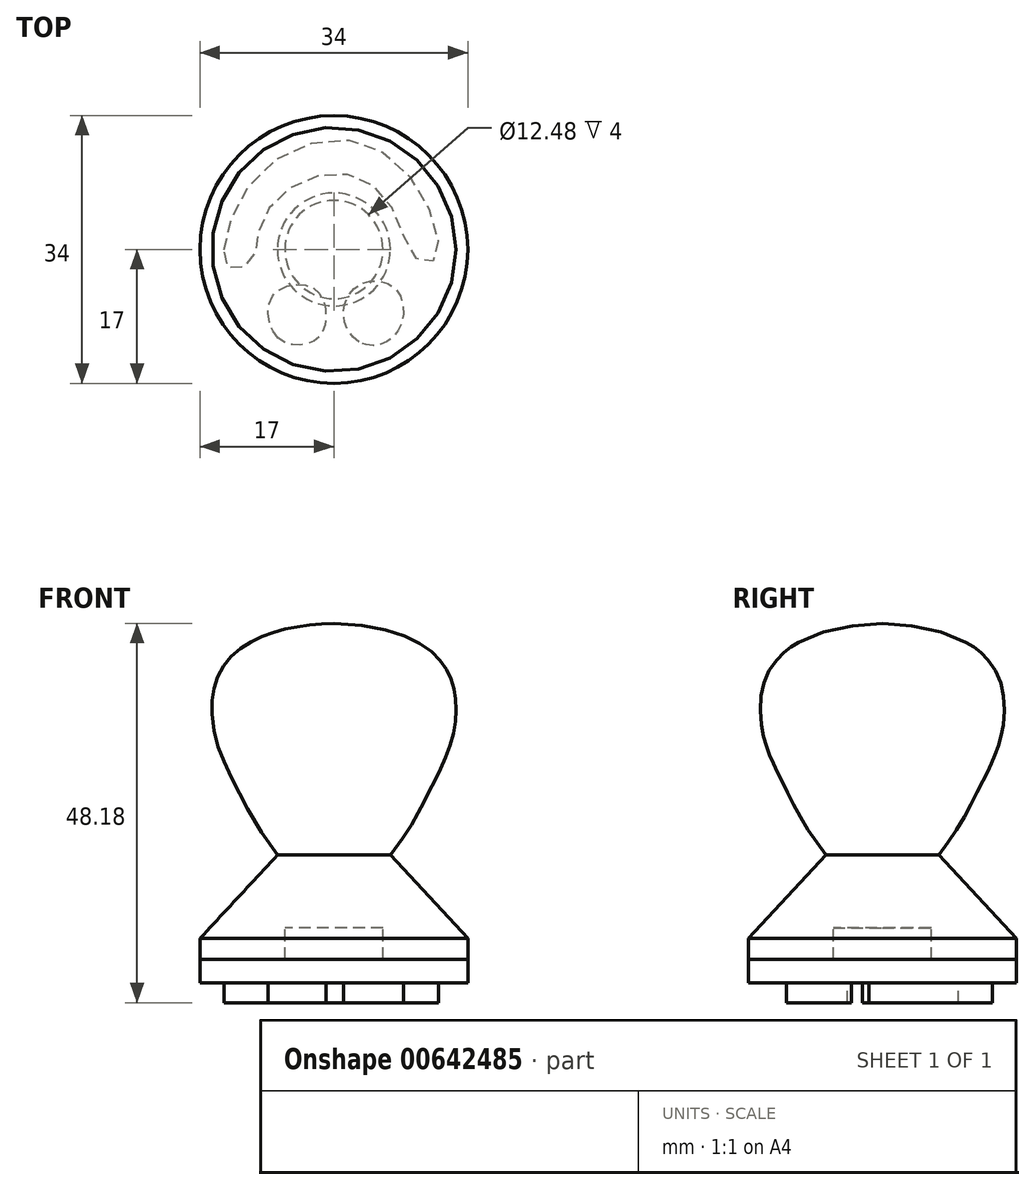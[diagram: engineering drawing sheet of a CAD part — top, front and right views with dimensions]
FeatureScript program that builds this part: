
annotation { "Feature Type Name" : "Feature", "Feature Type Description" : "" }
export const myFeature = defineFeature(function(context is Context, id is Id, definition is map)
    precondition{}
    {
        {
            var Q0;
            Q0=qCreatedBy(makeId("Front.planeOp"),FACE);
            var sketch = newSketch(context, id + "F0", { "sketchPlane" : qUnion([Q0])});
            skFitSpline(sketch, "E0", {"points": [v(0, 52.6) * mm, v(13.73, 47.6) * mm, v(15.4, 43.34) * mm, v(14.92, 37.64) * mm, v(12.14, 31.33) * mm, v(7.17, 23.18) * mm], "startDerivative": vector(89.4, -2.75) * mm, "endDerivative": vector(-39.97, -53.3) * mm});
            skLineSegment(sketch, "E1", {"start": v(7.17, 23.18) * mm, "end": v(17, 12.6) * mm});
            skLineSegment(sketch, "E2", {"start": v(17, 12.6) * mm, "end": v(0, 12.6) * mm});
            skLineSegment(sketch, "E3", {"start": v(0, 12.6) * mm, "end": v(0, 52.6) * mm});
            skLineSegment(sketch, "E4", {"start": v(17, 12.6) * mm, "end": v(5.53, 12.6) * mm});
            skLineSegment(sketch, "E5", {"start": v(5.53, 12.6) * mm, "end": v(5.53, 16.54) * mm});
            skLineSegment(sketch, "E6", {"start": v(5.53, 16.54) * mm, "end": v(0, 16.54) * mm});
            skLineSegment(sketch, "E7", {"start": v(0, 16.54) * mm, "end": v(0, 9.76) * mm});
            skLineSegment(sketch, "E8", {"start": v(0, 9.76) * mm, "end": v(17, 9.76) * mm});
            skLineSegment(sketch, "E9", {"start": v(17, 9.76) * mm, "end": v(17, 12.6) * mm});
            skSolve(sketch);
        }
        {
            var Q0;
            Q0 = qSketchRegion(id + "F0", true);
            var Q1;
            Q1=sQuery(id+"F0.wireOp",EDGE,"E3");
            revolve(context, id + "F1", {"entities" : qUnion([Q0]), "axis" : qUnion([Q1]), "revolveType" : RevolveType.FULL});
        }
        {
            var Q0;
            Q0=qCreatedBy(makeId("Front.planeOp"),FACE);
            var sketch = newSketch(context, id + "F2", { "sketchPlane" : qUnion([Q0])});
            skLineSegment(sketch, "E10", {"start": v(0, 6.93) * mm, "end": v(17, 6.93) * mm});
            skLineSegment(sketch, "E11", {"start": v(17, 6.93) * mm, "end": v(17, 9.93) * mm});
            skLineSegment(sketch, "E12", {"start": v(17, 9.93) * mm, "end": v(6.24, 9.93) * mm});
            skLineSegment(sketch, "E13", {"start": v(6.24, 9.93) * mm, "end": v(6.24, 13.93) * mm});
            skLineSegment(sketch, "E14", {"start": v(6.24, 13.93) * mm, "end": v(0, 13.93) * mm});
            skLineSegment(sketch, "E15", {"start": v(0, 13.93) * mm, "end": v(0, 6.93) * mm});
            skSolve(sketch);
        }
        {
            var Q0;
            Q0 = qSketchRegion(id + "F2", true);
            var Q1;
            Q1=sQuery(id+"F2.wireOp",EDGE,"E15");
            revolve(context, id + "F3", {"entities" : qUnion([Q0]), "axis" : qUnion([Q1]), "revolveType" : RevolveType.FULL});
        }
        {
            var Q0;
            Q0=makeQuery(id+"F3.opRevolve","SWEPT_FACE",FACE,{"disambiguationData":[OSD([sQuery(id+"F2.wireOp",EDGE,"E10")])]});
            var sketch = newSketch(context, id + "F4", { "sketchPlane" : qUnion([Q0])});
            skFitSpline(sketch, "E16", {"points": [v(-13.93, 0) * mm, v(-9.39, -9.76) * mm, v(2.72, -13.78) * mm, v(11.54, -6.28) * mm, v(12.86, 1.21) * mm, v(10.55, 1.21) * mm, v(7.37, -5.35) * mm, v(1.64, -9.54) * mm, v(-6.08, -7.45) * mm, v(-9.63, -2.1) * mm, v(-10.5, 1.49) * mm, v(-13.14, 2.48) * mm, v(-13.93, 0) * mm]});
            skFitSpline(sketch, "E17", {"points": [v(-7.1, 11.25) * mm, v(-7.77, 5.85) * mm, v(-2.53, 4.96) * mm, v(-1.1, 9.4) * mm, v(-3, 11.83) * mm, v(-7.1, 11.25) * mm]});
            skFitSpline(sketch, "E18", {"points": [v(3.18, 11.74) * mm, v(1.2, 8.32) * mm, v(3.4, 4.35) * mm, v(7.79, 4.96) * mm, v(8.58, 9.42) * mm, v(6.16, 11.96) * mm, v(3.18, 11.74) * mm]});
            skSolve(sketch);
        }
        {
            var Q0;
            Q0 = qSketchRegion(id + "F4", true);
            extrude(context, id + "F5", {"entities" : qUnion([Q0]), "operationType" : NewBodyOperationType.ADD, "depth" : 2.5 * mm, "offsetDistance" : 25 * mm});
        }
        {
            var Q0;
            Q0=makeQuery(id+"F3.opRevolve","SWEPT_BODY",BODY,{"disambiguationData":[OSD([sQuery(id+"F2.wireOp",EDGE,"E10"),sQuery(id+"F2.wireOp",EDGE,"E11"),sQuery(id+"F2.wireOp",EDGE,"E12"),sQuery(id+"F2.wireOp",EDGE,"E13"),sQuery(id+"F2.wireOp",EDGE,"E14"),sQuery(id+"F2.wireOp",EDGE,"E15")])]});
            var Q1;
            Q1=makeQuery(id+"F1.opRevolve","SWEPT_BODY",BODY,{"disambiguationData":[OSD([sQuery(id+"F0.wireOp",EDGE,"E0"),sQuery(id+"F0.wireOp",EDGE,"E1"),sQuery(id+"F0.wireOp",EDGE,"E3"),sQuery(id+"F0.wireOp",EDGE,"E7"),sQuery(id+"F0.wireOp",EDGE,"E8"),sQuery(id+"F0.wireOp",EDGE,"E9")])]});
            booleanBodies(context, id + "F6", {"operationType" : BooleanOperationType.SUBTRACTION, "tools" : qUnion([Q0]), "targets" : qUnion([Q1]), "keepTools" : true});
        }
    });
